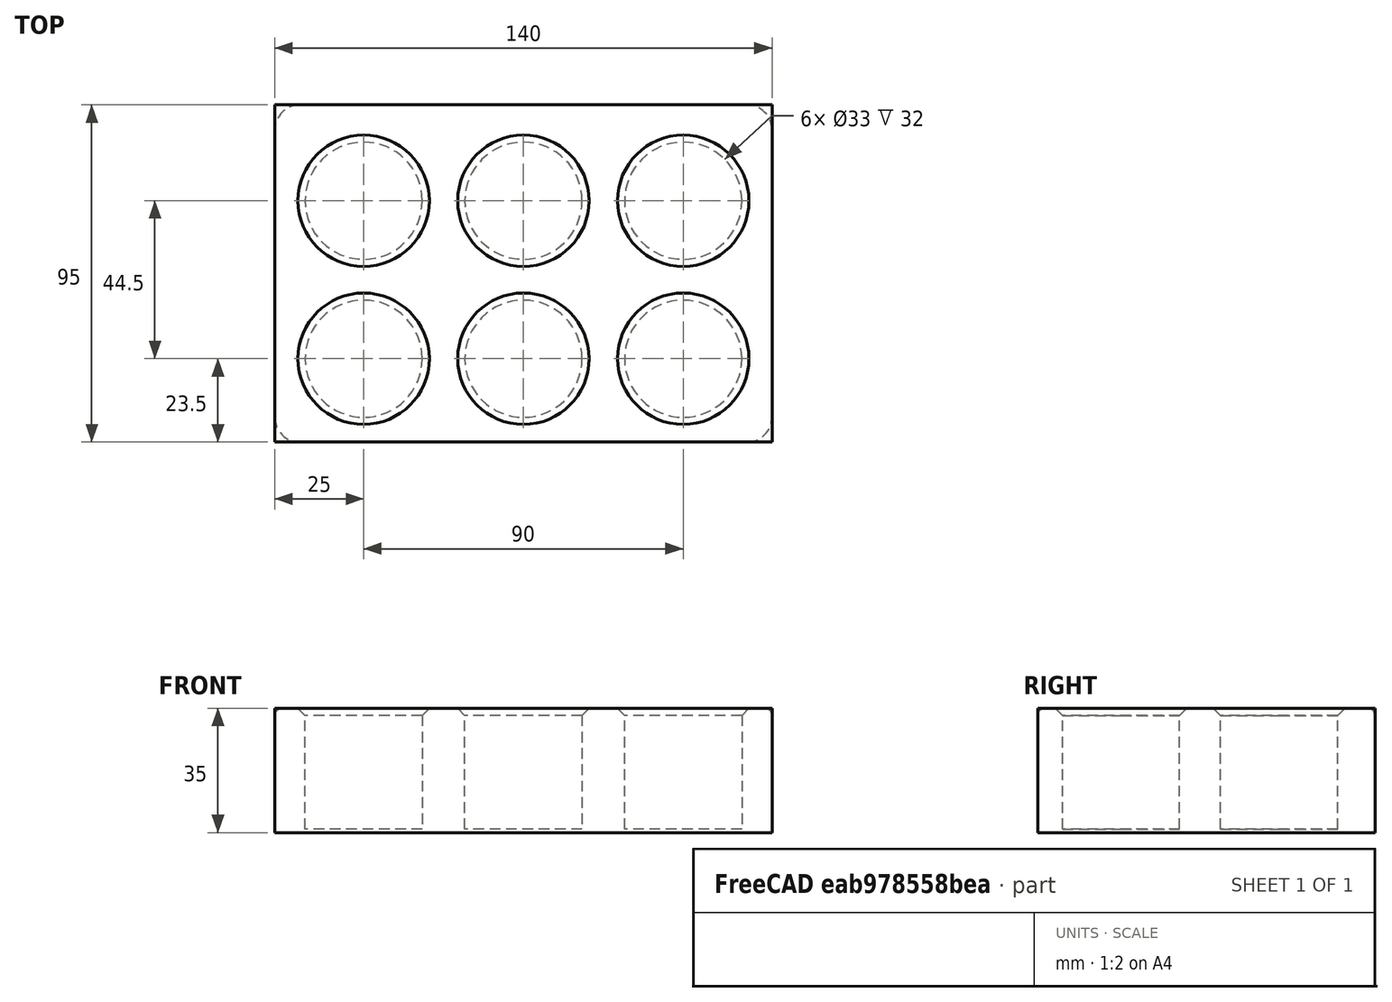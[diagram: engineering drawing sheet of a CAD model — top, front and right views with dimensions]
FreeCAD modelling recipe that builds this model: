
FCSTD DOCUMENT  (FreeCAD 0.16R)
Label: 5Crack
License: All rights reserved
LicenseURL: http://en.wikipedia.org/wiki/All_rights_reserved
objects: Sketcher::SketchObject×2, PartDesign::Fillet×2, PartDesign::Pad×1, PartDesign::Pocket×1, PartDesign::Chamfer×1, Mesh::Feature×1
note: 9 computed .brp shape members not serialized (recipe doc carries the construction recipe); baked Part::Feature solids carry a one-line shape summary decoded from their .brp

FEATURE [Sketcher::SketchObject] Sketch
  sketch-geometry (4):
    g0: LineSegment StartX=-70 StartY=47.5 StartZ=0 EndX=70 EndY=47.5 EndZ=0
    g1: LineSegment StartX=70 StartY=47.5 StartZ=0 EndX=70 EndY=-47.5 EndZ=0
    g2: LineSegment StartX=70 StartY=-47.5 StartZ=0 EndX=-70 EndY=-47.5 EndZ=0
    g3: LineSegment StartX=-70 StartY=-47.5 StartZ=0 EndX=-70 EndY=47.5 EndZ=0
  constraints (11):
    c: Coincident(g0,g1)
    c: Coincident(g1,g2)
    c: Coincident(g2,g3)
    c: Coincident(g3,g0)
    c: Horizontal(g0)
    c: Horizontal(g2)
    c: Vertical(g1)
    c: Vertical(g3)
    c: Symmetric(g1,g0,g-1)
    c: Distance(g3) = 95
    c: Distance(g0) = 140
FEATURE [PartDesign::Pad] Pad
  Length = 35
  Length2 = 100
  Sketch = -> Sketch
  Type = 0
FEATURE [Sketcher::SketchObject] Sketch001
  Placement = pos=(0,0,35) rot=(0,0,1;0rad)
  Support = -> Pad [Face6]
  sketch-geometry (12):
    g0: Circle [constr] CenterX=-45 CenterY=20.5 CenterZ=0 NormalX=0 NormalY=0 NormalZ=1 Radius=20.5
    g1: Circle [constr] CenterX=45 CenterY=-24 CenterZ=0 NormalX=0 NormalY=0 NormalZ=1 Radius=20.5
    g2: Circle [constr] CenterX=0 CenterY=20.5 CenterZ=0 NormalX=0 NormalY=0 NormalZ=1 Radius=20.5
    g3: Circle [constr] CenterX=45 CenterY=20.5 CenterZ=0 NormalX=0 NormalY=0 NormalZ=1 Radius=20.5
    g4: Circle [constr] CenterX=0 CenterY=-24 CenterZ=0 NormalX=0 NormalY=0 NormalZ=1 Radius=20.5
    g5: Circle [constr] CenterX=-45 CenterY=-24 CenterZ=0 NormalX=0 NormalY=0 NormalZ=1 Radius=20.5
    g6: Circle CenterX=-45 CenterY=20.5 CenterZ=0 NormalX=0 NormalY=0 NormalZ=1 Radius=16.5
    g7: Circle CenterX=0 CenterY=20.5 CenterZ=0 NormalX=0 NormalY=0 NormalZ=1 Radius=16.5
    g8: Circle CenterX=45 CenterY=20.5 CenterZ=0 NormalX=0 NormalY=0 NormalZ=1 Radius=16.5
    g9: Circle CenterX=45 CenterY=-24 CenterZ=0 NormalX=0 NormalY=0 NormalZ=1 Radius=16.5
    g10: Circle CenterX=0 CenterY=-24 CenterZ=0 NormalX=0 NormalY=0 NormalZ=1 Radius=16.5
    g11: Circle CenterX=-45 CenterY=-24 CenterZ=0 NormalX=0 NormalY=0 NormalZ=1 Radius=16.5
  constraints (23):
    c: Radius(g1) = 20.5
    c: Equal(g1,g0)
    c: Equal(g1, g2-g5) x4
    c: PointOnObject(g2,g-2)
    c: PointOnObject(g4,g-2)
    c: Tangent(g0,g-1)
    c: Tangent(g2,g-1)
    c: Tangent(g-1,g3)
    c: DistanceX(g3) = 45
    c: DistanceX(g0) = -45
    c: DistanceX(g5) = -45
    c: DistanceX(g1) = 45
    c: DistanceY(g1) = -24
    c: DistanceY(g4) = -24
    c: DistanceY(g5) = -24
    c: Radius(g6) = 16.5
    c: Equal(g6, g7-g11) x5
    c: Coincident(g6,g0)
    c: Coincident(g7,g2)
    c: Coincident(g8,g3)
    c: Coincident(g9,g1)
    c: Coincident(g11,g5)
    c: Coincident(g10,g4)
FEATURE [PartDesign::Pocket] Pocket
  Length = 34
  Sketch = -> Sketch001
  Type = 0
FEATURE [PartDesign::Fillet] Fillet
  Base = -> Pocket [Edge5,Edge8,Edge2,Edge1]
  Radius = 7
FEATURE [PartDesign::Fillet] Fillet001
  Base = -> Fillet [Edge20,Edge16,Edge4,Edge17]
  Radius = 2
FEATURE [PartDesign::Chamfer] Chamfer
  Base = -> Fillet001 [Edge34,Edge33,Edge30,Edge29,Edge31,Edge32]
  Size = 2
FEATURE [Mesh::Feature] Mesh  label="Chamfer (Meshed)"
